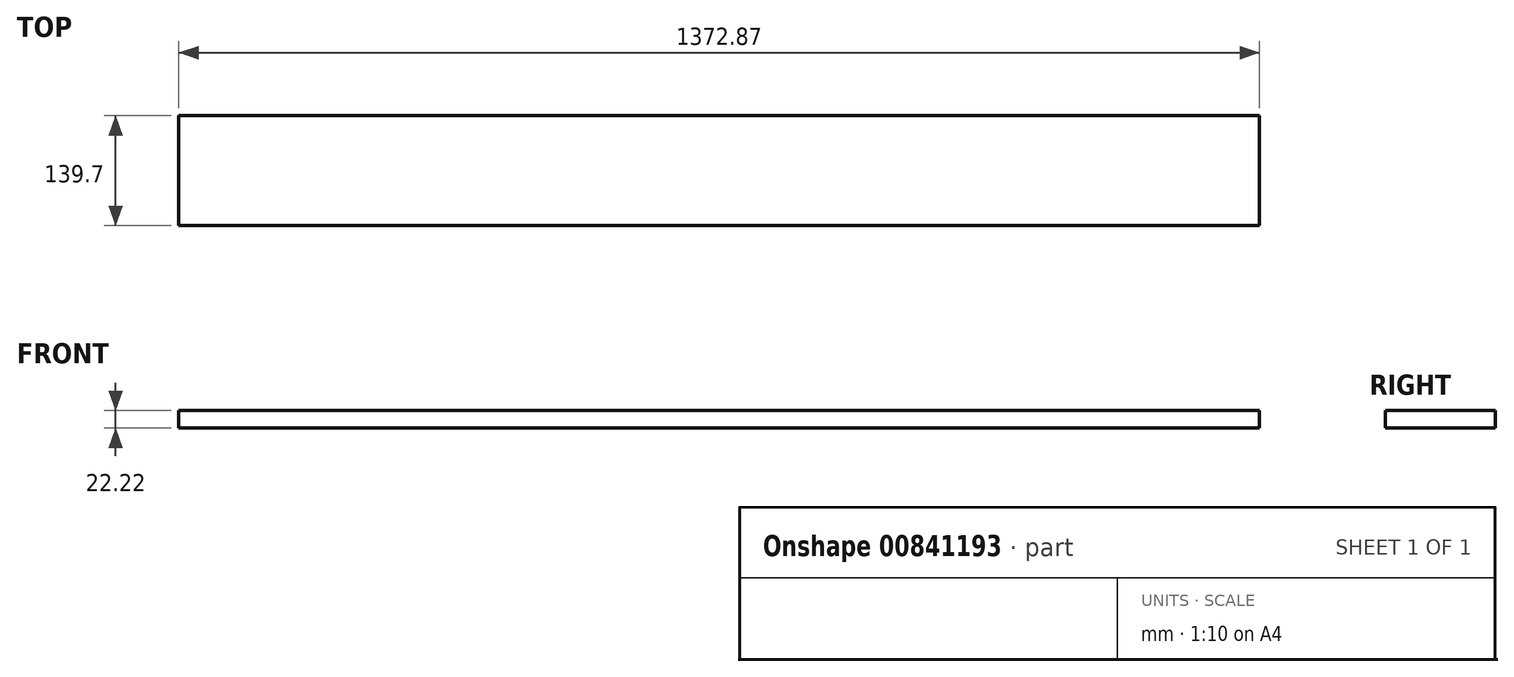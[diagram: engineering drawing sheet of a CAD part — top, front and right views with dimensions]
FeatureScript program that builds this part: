
annotation { "Feature Type Name" : "Feature", "Feature Type Description" : "" }
export const myFeature = defineFeature(function(context is Context, id is Id, definition is map)
    precondition{}
    {
        {
            var Q0;
            Q0=qCreatedBy(makeId("Right.planeOp"),FACE);
            var sketch = newSketch(context, id + "F0", { "sketchPlane" : qUnion([Q0])});
            skLineSegment(sketch, "E0.bottom", {"start": v(69.85, -11.11) * mm, "end": v(-69.85, -11.11) * mm});
            skLineSegment(sketch, "E0.top", {"start": v(69.85, 11.11) * mm, "end": v(-69.85, 11.11) * mm});
            skLineSegment(sketch, "E0.left", {"start": v(69.85, -11.11) * mm, "end": v(69.85, 11.11) * mm});
            skLineSegment(sketch, "E0.right", {"start": v(-69.85, -11.11) * mm, "end": v(-69.85, 11.11) * mm});
            skPoint(sketch, "E0.middle", {"position": v(0, 0) * mm});
            skSolve(sketch);
        }
        {
            var Q0;
            Q0=makeQuery(id+"F0.imprint","IMPRINT",FACE,{"disambiguationData":[TD([[makeQuery(id+"F0.imprint","IMPRINT",EDGE,{"derivedFrom":sQuery(id+"F0.wireOp",EDGE,"E0.bottom")}),-1.0]])]});
            extrude(context, id + "F1", {"entities" : qUnion([Q0]), "depth" : 1372.87 * mm, "offsetDistance" : 25.4 * mm});
        }
    });
